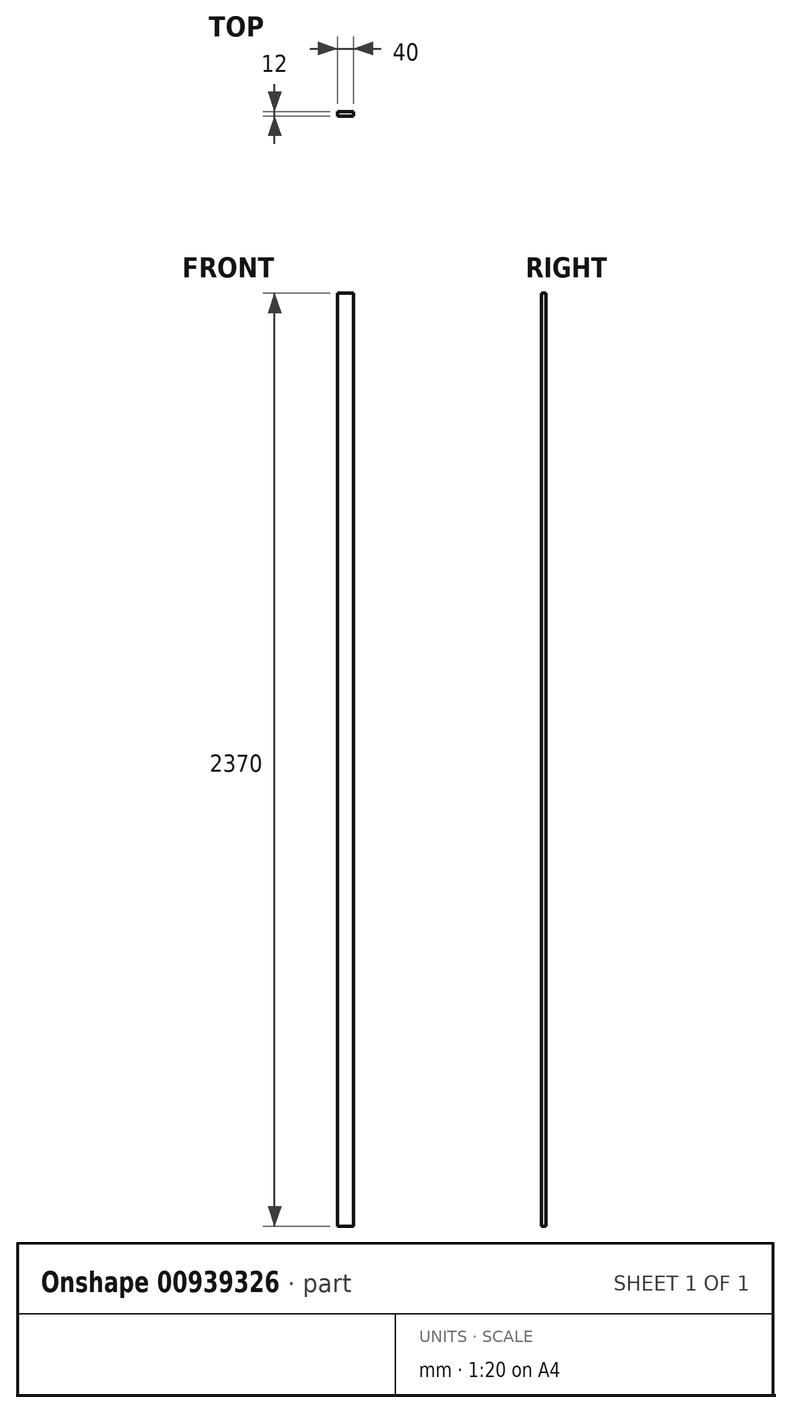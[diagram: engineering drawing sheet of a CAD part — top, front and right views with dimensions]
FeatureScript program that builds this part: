
annotation { "Feature Type Name" : "Feature", "Feature Type Description" : "" }
export const myFeature = defineFeature(function(context is Context, id is Id, definition is map)
    precondition{}
    {
        {
            var Q0;
            Q0=qCreatedBy(makeId("Front.planeOp"),FACE);
            var sketch = newSketch(context, id + "F0", { "sketchPlane" : qUnion([Q0])});
            skLineSegment(sketch, "E0.bottom", {"start": v(0, 0) * mm, "end": v(-40, 0) * mm});
            skLineSegment(sketch, "E0.top", {"start": v(0, 2370) * mm, "end": v(-40, 2370) * mm});
            skLineSegment(sketch, "E0.left", {"start": v(0, 0) * mm, "end": v(0, 2370) * mm});
            skLineSegment(sketch, "E0.right", {"start": v(-40, 0) * mm, "end": v(-40, 2370) * mm});
            skSolve(sketch);
        }
        {
            var Q0;
            Q0 = qSketchRegion(id + "F0", true);
            extrude(context, id + "F1", {"entities" : qUnion([Q0]), "depth" : 12 * mm, "offsetDistance" : 25 * mm});
        }
    });
